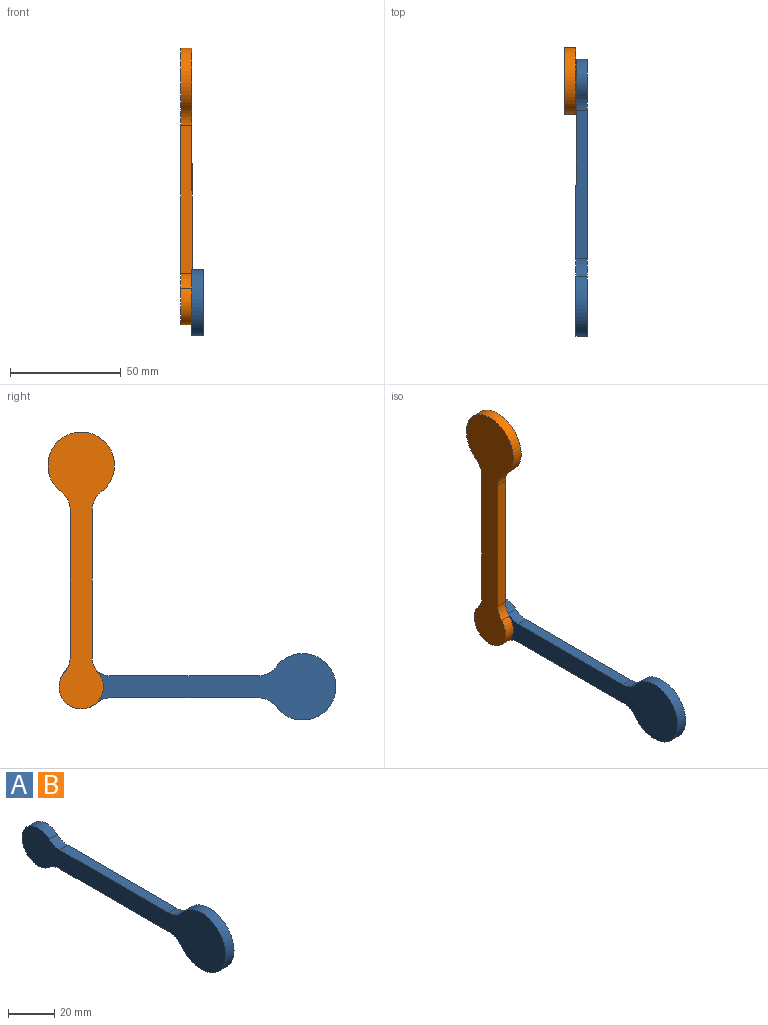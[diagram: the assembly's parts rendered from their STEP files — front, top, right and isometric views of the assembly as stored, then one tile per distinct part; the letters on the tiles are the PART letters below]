
ASSEMBLY  parts=2 mates=1
PART A: 10 faces, bbox 5x125x30 mm
  f0: cylinder r=15mm len=30mm, axis (1,0,0), area 374.7mm2, adj f1,f7,f8,f9
  f1: cylinder r=10mm len=8mm, axis (1,0,0), area 46.4mm2, adj f0,f2,f8,f9
  f2: plane 66.77x5mm, normal (0,0,-1), area 333.9mm2, adj f1,f3,f8,f9
  f3: cylinder r=10mm len=6.61mm, axis (1,0,0), area 36.1mm2, adj f2,f4,f8,f9
  f4: cylinder r=10mm len=20mm, axis (1,0,0), area 229.4mm2, adj f3,f5,f8,f9
  f5: cylinder r=10mm len=6.61mm, axis (1,0,0), area 36.1mm2, adj f4,f6,f8,f9
  f6: plane 66.77x5mm, normal (0,0,1), area 333.9mm2, adj f5,f7,f8,f9
  f7: cylinder r=10mm len=8mm, axis (1,0,0), area 46.4mm2, adj f0,f6,f8,f9
  f8: plane 125x30mm, normal (-1,0,0), area 1792.6mm2, adj f0,f1,f2,f3,f4,f5,f6,f7
  f9: plane 125x30mm, normal (1,0,0), area 1792.6mm2, adj f0,f1,f2,f3,f4,f5,f6,f7
PART B: same geometry as A
PLACE A t=(-18.8,10.58,-9.56)mm
PLACE B rot(axis=(0,0.71,-0.71),180deg) t=(-18.8,110.58,90.44)mm
MATE revolute A.f4 <-> B.f4  axis (-1,0,0) through (-18.8,110.58,-9.56)mm
